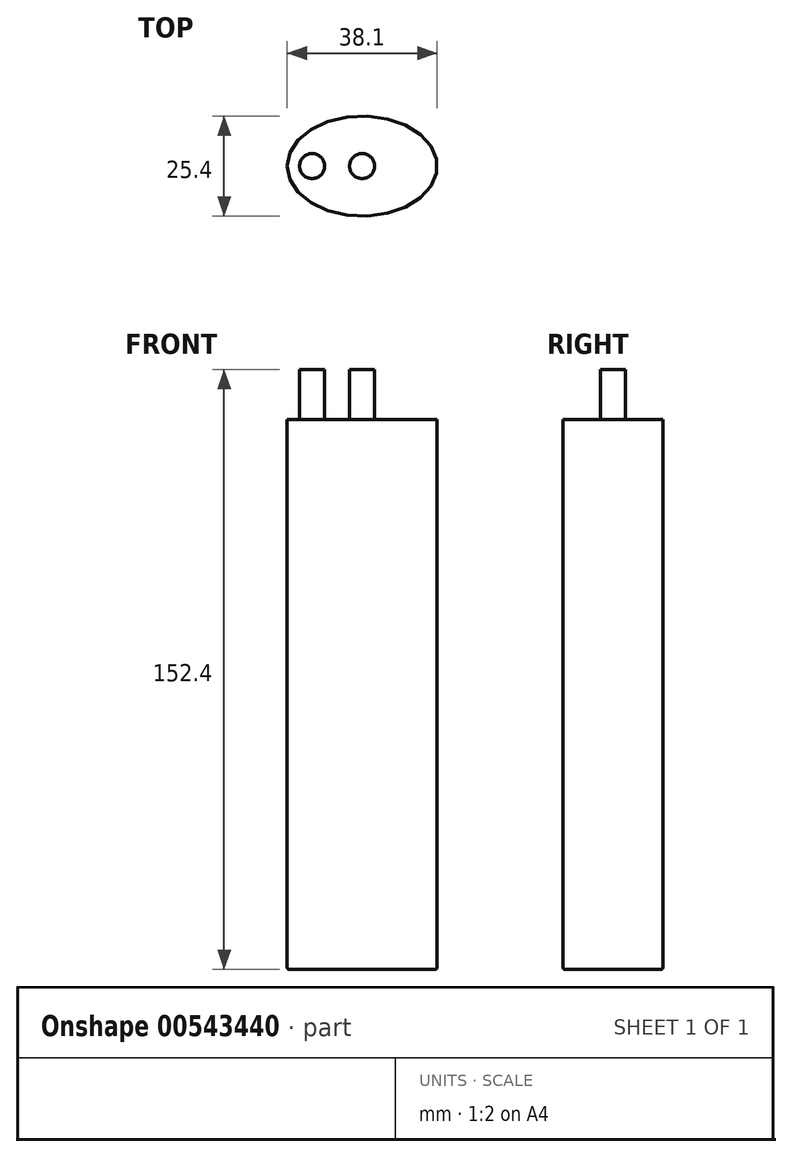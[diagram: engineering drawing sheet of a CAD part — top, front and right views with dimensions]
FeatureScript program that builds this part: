
annotation { "Feature Type Name" : "Feature", "Feature Type Description" : "" }
export const myFeature = defineFeature(function(context is Context, id is Id, definition is map)
    precondition{}
    {
        {
            var Q0;
            Q0=qCreatedBy(makeId("Top.planeOp"),FACE);
            var sketch = newSketch(context, id + "F0", { "sketchPlane" : qUnion([Q0])});
            skLineSegment(sketch, "E0", {"start": v(0, 0) * mm, "end": v(-19.05, 0) * mm});
            skEllipse(sketch, "E1", {"center": v(0, 0) * mm, "majorRadius": 19.05 * mm, "minorRadius": 12.7 * mm, "majorAxis": v(-1, 0)});
            skLineSegment(sketch, "E2", {"start": v(0, 0) * mm, "end": v(0, -12.7) * mm});
            skSolve(sketch);
        }
        {
            var Q0;
            {var subQ0=sQuery(id+"F0.wireOp",EDGE,"E0");Q0=makeQuery(id+"F0.imprint","IMPRINT",FACE,{"disambiguationData":[TD([[makeQuery(id+"F0.imprint","IMPRINT",EDGE,{"derivedFrom":subQ0}),-1.0]])]});}
            var Q1;
            {var subQ0=sQuery(id+"F0.wireOp",EDGE,"E0");Q1=makeQuery(id+"F0.imprint","IMPRINT",FACE,{"disambiguationData":[TD([[makeQuery(id+"F0.imprint","IMPRINT",EDGE,{"derivedFrom":subQ0}),1.0]])]});}
            extrude(context, id + "F1", {"entities" : qUnion([Q0, Q1]), "depth" : 139.7 * mm, "offsetDistance" : 25.4 * mm});
        }
        {
            var Q0;
            Q0=makeQuery(id+"F1.opExtrude","CAP_FACE",FACE,{"disambiguationData":[OSD([sQuery(id+"F0.wireOp",EDGE,"E1")])],"isStart":false});
            var sketch = newSketch(context, id + "F2", { "sketchPlane" : qUnion([Q0])});
            skLineSegment(sketch, "E3", {"start": v(0, 0) * mm, "end": v(-12.7, 0) * mm});
            skCircle(sketch, "E4", {"center": v(0, 0) * mm, "radius": 3.18 * mm});
            skCircle(sketch, "E5", {"center": v(-12.7, 0) * mm, "radius": 3.18 * mm});
            skSolve(sketch);
        }
        {
            var Q0;
            Q0=makeQuery(id+"F2.imprint","IMPRINT",FACE,{"disambiguationData":[TD([[makeQuery(id+"F2.imprint","IMPRINT",EDGE,{"derivedFrom":sQuery(id+"F2.wireOp",EDGE,"E5")}),1.0]])]});
            var Q1;
            Q1=makeQuery(id+"F2.imprint","IMPRINT",FACE,{"disambiguationData":[TD([[makeQuery(id+"F2.imprint","IMPRINT",EDGE,{"derivedFrom":sQuery(id+"F2.wireOp",EDGE,"E4")}),1.0]])]});
            extrude(context, id + "F3", {"entities" : qUnion([Q0, Q1]), "operationType" : NewBodyOperationType.ADD, "depth" : 12.7 * mm, "offsetDistance" : 25.4 * mm});
        }
        {
            var Q0;
            Q0=makeQuery(id+"F1.opExtrude","CAP_EDGE",EDGE,{"disambiguationData":[OSD([sQuery(id+"F0.wireOp",EDGE,"E1")])],"isStart":true});
            fillet(context, id + "F4", {"entities" : qUnion([Q0]), "radius" : 0.5 * mm, "tangentPropagation" : true, "allowEdgeOverflow" : false});
        }
    });
